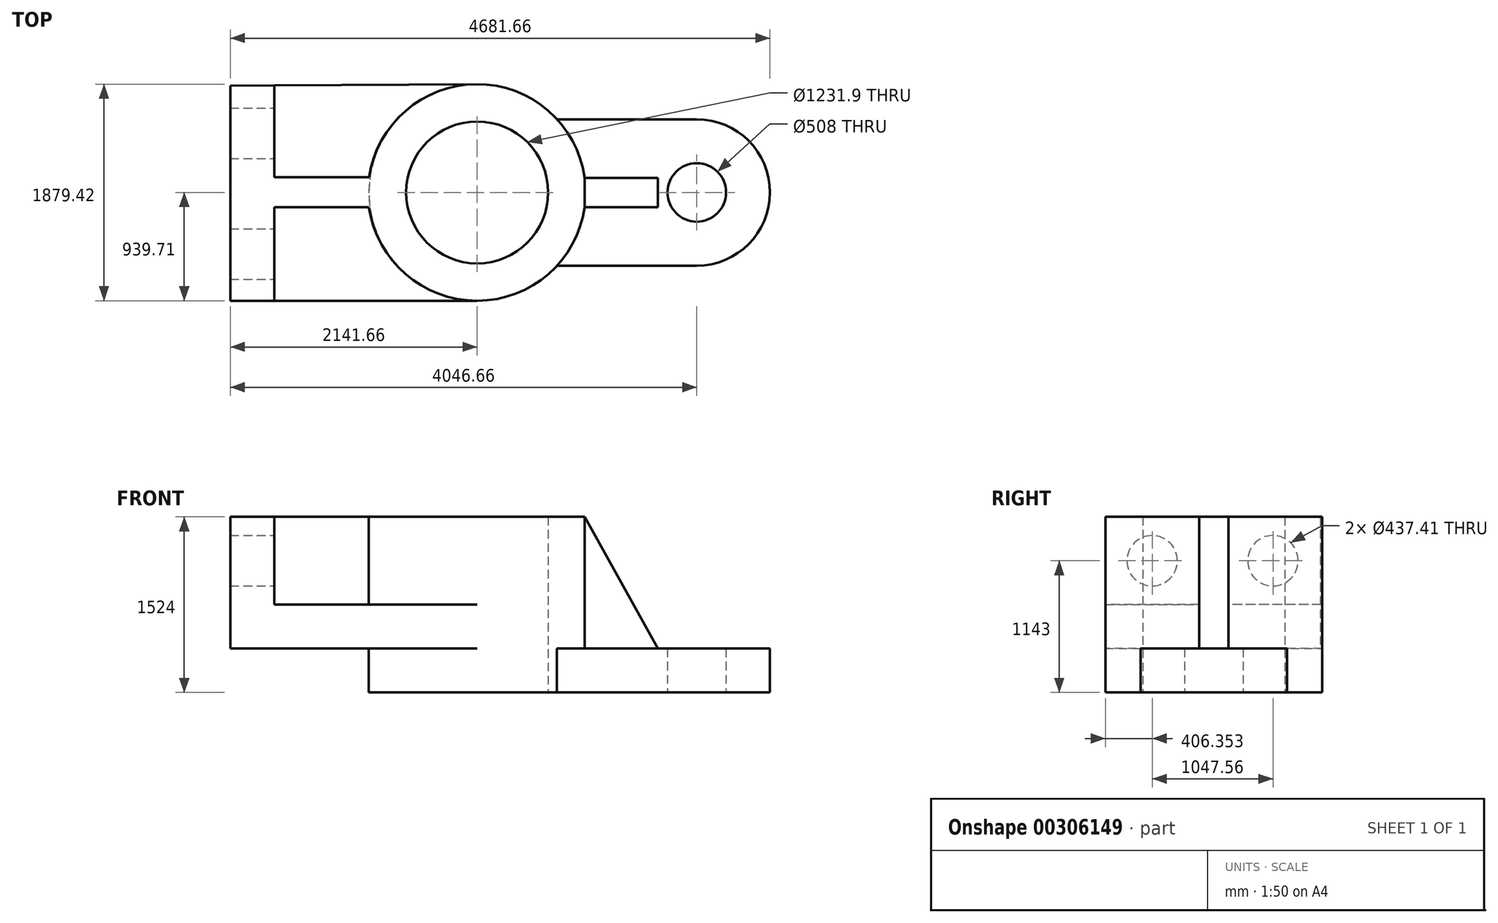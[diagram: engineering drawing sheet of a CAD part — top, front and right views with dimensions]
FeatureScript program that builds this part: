
annotation { "Feature Type Name" : "Feature", "Feature Type Description" : "" }
export const myFeature = defineFeature(function(context is Context, id is Id, definition is map)
    precondition{}
    {
        {
            var Q0;
            Q0=qCreatedBy(makeId("Top.planeOp"),FACE);
            var sketch = newSketch(context, id + "F0", { "sketchPlane" : qUnion([Q0])});
            skCircle(sketch, "E0", {"center": v(0, 0) * mm, "radius": 615.95 * mm});
            skCircle(sketch, "E1", {"center": v(0, 0) * mm, "radius": 939.71 * mm});
            skCircle(sketch, "E2", {"center": v(1905, 0) * mm, "radius": 254 * mm});
            skCircle(sketch, "E3", {"center": v(1905, 0) * mm, "radius": 635 * mm});
            skLineSegment(sketch, "E4", {"start": v(1905, 635) * mm, "end": v(692.7, 635) * mm});
            skLineSegment(sketch, "E5", {"start": v(1905, -635) * mm, "end": v(692.7, -635) * mm});
            skLineSegment(sketch, "E6", {"start": v(1566.1, 0) * mm, "end": v(1566.1, 127) * mm});
            skLineSegment(sketch, "E7", {"start": v(1566.1, 127) * mm, "end": v(931.1, 127) * mm});
            skLineSegment(sketch, "E8", {"start": v(1566.1, 0) * mm, "end": v(1566.1, -127) * mm});
            skLineSegment(sketch, "E9", {"start": v(1566.1, -127) * mm, "end": v(931.1, -127) * mm});
            skSolve(sketch);
        }
        {
            var Q0;
            Q0=makeQuery(id+"F0.imprint","IMPRINT",FACE,{"disambiguationData":[TD([[makeQuery(id+"F0.imprint","IMPRINT",EDGE,{"derivedFrom":sQuery(id+"F0.wireOp",EDGE,"E0")}),-1.0]])]});
            var Q1;
            {var subQ0=sQuery(id+"F0.wireOp",EDGE,"E7");var subQ1=sQuery(id+"F0.wireOp",EDGE,"E1");var subQ2=makeQuery(id+"F0.imprint","INTERSECT",VERTEX,{"derivedFrom":[subQ1,subQ0]});Q1=makeQuery(id+"F0.imprint","IMPRINT",FACE,{"disambiguationData":[TD([[makeQuery(id+"F0.imprint","IMPRINT",EDGE,{"disambiguationData":[TD([[subQ2,1.0]])],"derivedFrom":subQ1}),-1.0]])]});}
            var Q2;
            {var subQ2=sQuery(id+"F0.wireOp",EDGE,"E6");Q2=makeQuery(id+"F0.imprint","IMPRINT",FACE,{"disambiguationData":[TD([[makeQuery(id+"F0.imprint","IMPRINT",EDGE,{"derivedFrom":subQ2}),1.0]])]});}
            extrude(context, id + "F1", {"entities" : qUnion([Q0, Q1, Q2]), "depth" : 1524 * mm});
        }
        {
            var Q0;
            {var subQ0=sQuery(id+"F0.wireOp",EDGE,"E4");Q0=makeQuery(id+"F0.imprint","IMPRINT",FACE,{"disambiguationData":[TD([[makeQuery(id+"F0.imprint","IMPRINT",EDGE,{"derivedFrom":subQ0}),1.0]])]});}
            var Q1;
            Q1=makeQuery(id+"F0.imprint","IMPRINT",FACE,{"disambiguationData":[TD([[makeQuery(id+"F0.imprint","IMPRINT",EDGE,{"derivedFrom":sQuery(id+"F0.wireOp",EDGE,"E2")}),-1.0]])]});
            var Q2;
            {var subQ0=sQuery(id+"F0.wireOp",EDGE,"E5");Q2=makeQuery(id+"F0.imprint","IMPRINT",FACE,{"disambiguationData":[TD([[makeQuery(id+"F0.imprint","IMPRINT",EDGE,{"derivedFrom":subQ0}),-1.0]])]});}
            extrude(context, id + "F2", {"entities" : qUnion([Q0, Q1, Q2]), "operationType" : NewBodyOperationType.ADD, "depth" : 381 * mm});
        }
        {
            var Q0;
            Q0=makeQuery(id+"F1.opExtrude","SWEPT_FACE",FACE,{"disambiguationData":[OSD([sQuery(id+"F0.wireOp",EDGE,"E9")])]});
            var sketch = newSketch(context, id + "F3", { "sketchPlane" : qUnion([Q0])});
            skLineSegment(sketch, "E10", {"start": v(931.1, 1524) * mm, "end": v(1566.1, 381) * mm});
            skLineSegment(sketch, "E11", {"start": v(1566.1, 381) * mm, "end": v(1566.1, 1524) * mm});
            skLineSegment(sketch, "E12", {"start": v(1566.1, 1524) * mm, "end": v(931.1, 1524) * mm});
            skSolve(sketch);
        }
        {
            var Q0;
            Q0=makeQuery(id+"F3.imprint","IMPRINT",FACE,{"disambiguationData":[TD([[makeQuery(id+"F3.imprint","IMPRINT",EDGE,{"derivedFrom":sQuery(id+"F3.wireOp",EDGE,"E10")}),1.0]])]});
            extrude(context, id + "F4", {"entities" : qUnion([Q0]), "operationType" : NewBodyOperationType.REMOVE, "oppositeDirection" : true, "depth" : 254 * mm});
        }
        {
            var Q0;
            Q0=makeQuery(id+"F2.opExtrude","CAP_FACE",FACE,{"disambiguationData":[OSD([sQuery(id+"F0.wireOp",EDGE,"E1"),sQuery(id+"F0.wireOp",EDGE,"E2"),sQuery(id+"F0.wireOp",EDGE,"E3"),sQuery(id+"F0.wireOp",EDGE,"E4"),sQuery(id+"F0.wireOp",EDGE,"E5"),sQuery(id+"F0.wireOp",EDGE,"E6"),sQuery(id+"F0.wireOp",EDGE,"E7"),sQuery(id+"F0.wireOp",EDGE,"E8"),sQuery(id+"F0.wireOp",EDGE,"E9")])],"isStart":false});
            var sketch = newSketch(context, id + "F5", { "sketchPlane" : qUnion([Q0])});
            skArc(sketch, "E13.0", {"start": v(931.1, 127) * mm, "mid": v(-939.71, 0) * mm, "end": v(931.1, -127) * mm});
            skLineSegment(sketch, "E14", {"start": v(0, -939.71) * mm, "end": v(-2141.66, -939.71) * mm});
            skLineSegment(sketch, "E15", {"start": v(-2141.66, -939.71) * mm, "end": v(-2141.66, 925.4) * mm});
            skLineSegment(sketch, "E16", {"start": v(-2141.66, 925.4) * mm, "end": v(0, 939.74) * mm});
            skSolve(sketch);
        }
        {
            var Q0;
            {var subQ0=sQuery(id+"F5.wireOp",EDGE,"E14");Q0=makeQuery(id+"F5.imprint","IMPRINT",FACE,{"disambiguationData":[TD([[makeQuery(id+"F5.imprint","IMPRINT",EDGE,{"derivedFrom":subQ0}),-1.0]])]});}
            extrude(context, id + "F6", {"entities" : qUnion([Q0]), "operationType" : NewBodyOperationType.ADD, "depth" : 1143 * mm});
        }
        {
            var Q0;
            Q0=makeQuery(id+"F6.boolean.opBoolean","MERGE",FACE,{"derivedFrom":[makeQuery(id+"F1.opExtrude","CAP_FACE",FACE,{"disambiguationData":[OSD([sQuery(id+"F0.wireOp",EDGE,"E0"),sQuery(id+"F0.wireOp",EDGE,"E1"),sQuery(id+"F0.wireOp",EDGE,"E6"),sQuery(id+"F0.wireOp",EDGE,"E7"),sQuery(id+"F0.wireOp",EDGE,"E8"),sQuery(id+"F0.wireOp",EDGE,"E9")])],"isStart":false}),makeQuery(id+"F6.opExtrude","CAP_FACE",FACE,{"disambiguationData":[OSD([sQuery(id+"F5.wireOp",EDGE,"E13.0"),sQuery(id+"F5.wireOp",EDGE,"E14"),sQuery(id+"F5.wireOp",EDGE,"E15"),sQuery(id+"F5.wireOp",EDGE,"E16")])],"isStart":false})]});
            var sketch = newSketch(context, id + "F7", { "sketchPlane" : qUnion([Q0])});
            skArc(sketch, "E17", {"start": v(-949.28, 0) * mm, "mid": v(-667.87, -665.05) * mm, "end": v(0, -939.71) * mm});
            skLineSegment(sketch, "E18", {"start": v(0, -939.71) * mm, "end": v(-1758.64, -939.71) * mm});
            skLineSegment(sketch, "E19", {"start": v(-1758.64, -939.71) * mm, "end": v(-1758.64, -127) * mm});
            skLineSegment(sketch, "E20", {"start": v(-1758.64, -127) * mm, "end": v(-939.45, -127) * mm});
            skLineSegment(sketch, "E21", {"start": v(-1758.64, 927.97) * mm, "end": v(-1758.64, 132.63) * mm});
            skArc(sketch, "E22", {"start": v(-6.29, 939.7) * mm, "mid": v(-670.08, 662.82) * mm, "end": v(-949.28, 0) * mm});
            skLineSegment(sketch, "E23", {"start": v(-1758.64, 132.63) * mm, "end": v(-938.6, 132.63) * mm});
            skLineSegment(sketch, "E24", {"start": v(-6.29, 939.7) * mm, "end": v(-1758.64, 927.97) * mm});
            skSolve(sketch);
        }
        {
            var Q0;
            Q0=makeQuery(id+"F7.imprint","IMPRINT",FACE,{"disambiguationData":[TD([[makeQuery(id+"F7.imprint","IMPRINT",EDGE,{"derivedFrom":sQuery(id+"F7.wireOp",EDGE,"E21")}),1.0]])]});
            var Q1;
            {var subQ0=sQuery(id+"F7.wireOp",EDGE,"E18");Q1=makeQuery(id+"F7.imprint","IMPRINT",FACE,{"disambiguationData":[TD([[makeQuery(id+"F7.imprint","IMPRINT",EDGE,{"derivedFrom":subQ0}),-1.0]])]});}
            extrude(context, id + "F8", {"entities" : qUnion([Q0, Q1]), "operationType" : NewBodyOperationType.REMOVE, "oppositeDirection" : true, "depth" : 762 * mm});
        }
        {
            var Q0;
            Q0=makeQuery(id+"F8.boolean.opBoolean","COPY",FACE,{"derivedFrom":makeQuery(id+"F8.opExtrude","SWEPT_FACE",FACE,{"disambiguationData":[OSD([sQuery(id+"F7.wireOp",EDGE,"E19")])]})});
            var sketch = newSketch(context, id + "F9", { "sketchPlane" : qUnion([Q0])});
            skCircle(sketch, "E25", {"center": v(-533.36, 1143) * mm, "radius": 218.7 * mm});
            skPoint(sketch, "E25.centerSnap0", {"position": v(-533.36, 762) * mm});
            skCircle(sketch, "E26", {"center": v(514.2, 1143) * mm, "radius": 218.7 * mm});
            skSolve(sketch);
        }
        {
            var Q0;
            Q0=makeQuery(id+"F9.imprint","IMPRINT",FACE,{"disambiguationData":[TD([[makeQuery(id+"F9.imprint","IMPRINT",EDGE,{"derivedFrom":sQuery(id+"F9.wireOp",EDGE,"E26")}),1.0]])]});
            var Q1;
            Q1=makeQuery(id+"F9.imprint","IMPRINT",FACE,{"disambiguationData":[TD([[makeQuery(id+"F9.imprint","IMPRINT",EDGE,{"derivedFrom":sQuery(id+"F9.wireOp",EDGE,"E25")}),1.0]])]});
            extrude(context, id + "F10", {"entities" : qUnion([Q0, Q1]), "operationType" : NewBodyOperationType.REMOVE, "oppositeDirection" : true, "depth" : 2540 * mm});
        }
    });
